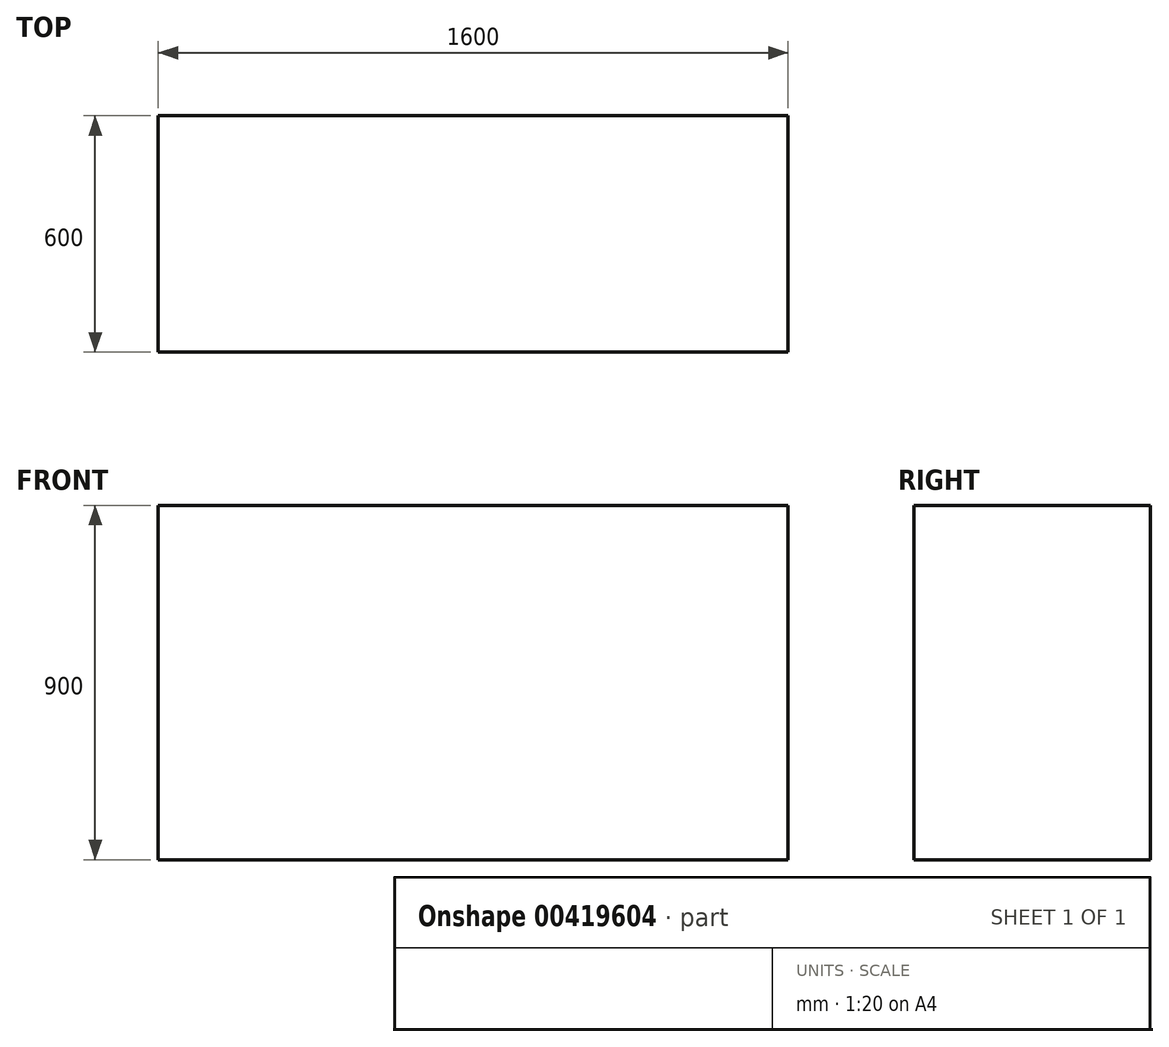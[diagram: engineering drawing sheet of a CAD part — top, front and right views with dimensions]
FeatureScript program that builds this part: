
annotation { "Feature Type Name" : "Feature", "Feature Type Description" : "" }
export const myFeature = defineFeature(function(context is Context, id is Id, definition is map)
    precondition{}
    {
        {
            var Q0;
            Q0=qCreatedBy(makeId("Top.planeOp"),FACE);
            var sketch = newSketch(context, id + "F0", { "sketchPlane" : qUnion([Q0])});
            skLineSegment(sketch, "E0.bottom", {"start": v(-1490.31, 550.53) * mm, "end": v(109.69, 550.53) * mm});
            skLineSegment(sketch, "E0.top", {"start": v(-1490.31, -49.47) * mm, "end": v(109.69, -49.47) * mm});
            skLineSegment(sketch, "E0.left", {"start": v(-1490.31, 550.53) * mm, "end": v(-1490.31, -49.47) * mm});
            skLineSegment(sketch, "E0.right", {"start": v(109.69, 550.53) * mm, "end": v(109.69, -49.47) * mm});
            skSolve(sketch);
        }
        {
            var Q0;
            Q0=makeQuery(id+"F0.imprint","IMPRINT",FACE,{"disambiguationData":[TD([[makeQuery(id+"F0.imprint","IMPRINT",EDGE,{"derivedFrom":sQuery(id+"F0.wireOp",EDGE,"E0.bottom")}),-1.0]])]});
            extrude(context, id + "F1", {"entities" : qUnion([Q0]), "depth" : 900 * mm});
        }
    });
